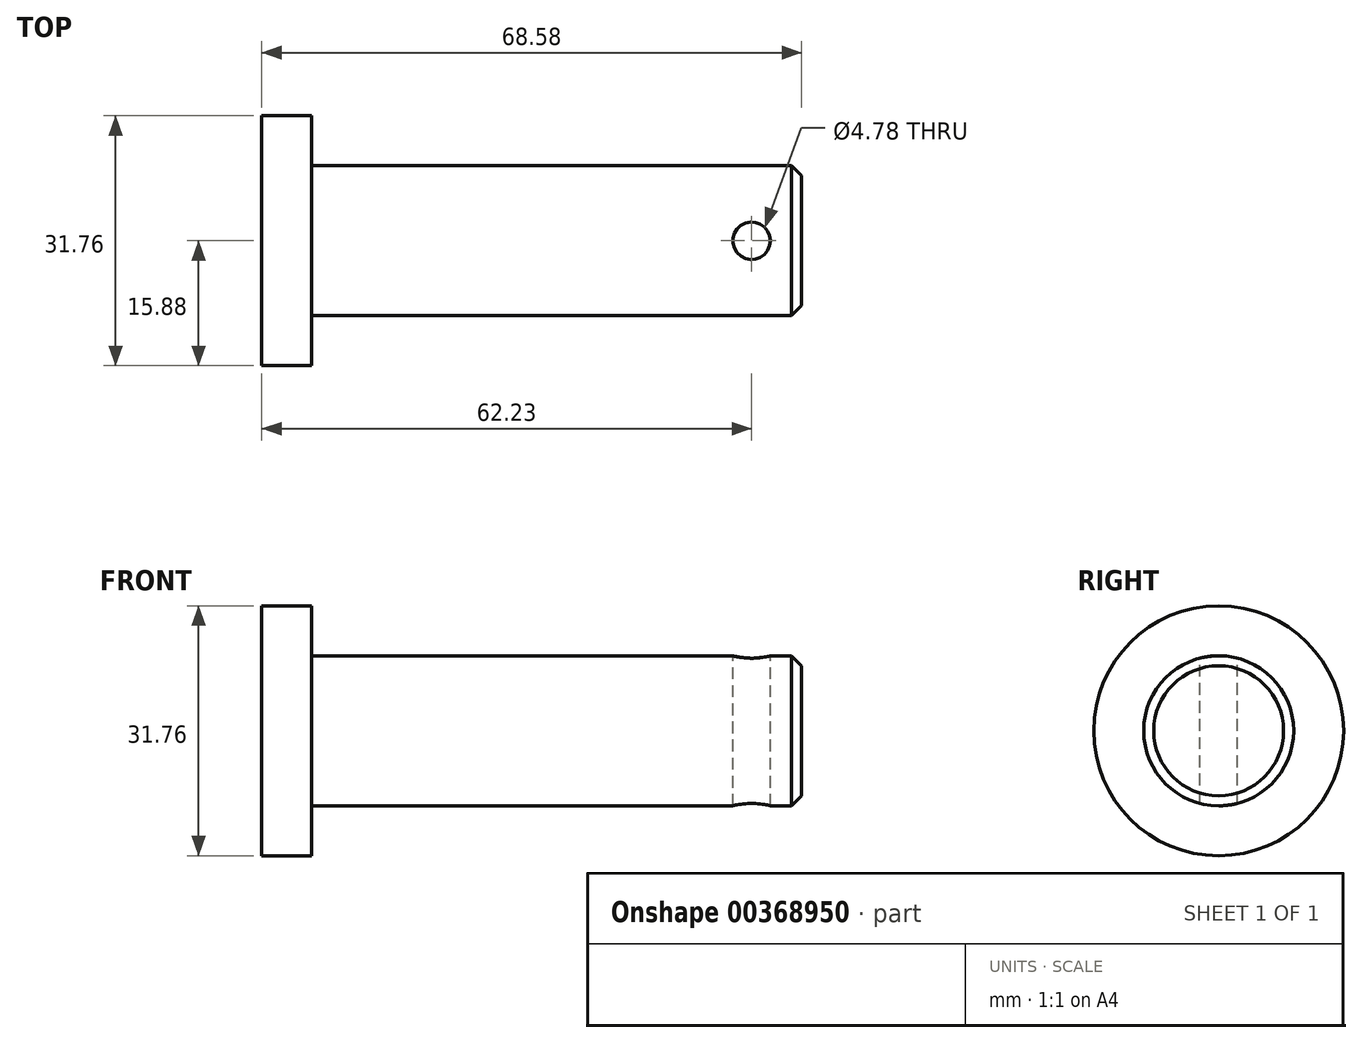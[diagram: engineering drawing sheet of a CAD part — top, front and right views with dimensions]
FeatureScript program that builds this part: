
annotation { "Feature Type Name" : "Feature", "Feature Type Description" : "" }
export const myFeature = defineFeature(function(context is Context, id is Id, definition is map)
    precondition{}
    {
        {
            var Q0;
            Q0=qCreatedBy(makeId("Right.planeOp"),FACE);
            var sketch = newSketch(context, id + "F0", { "sketchPlane" : qUnion([Q0])});
            skCircle(sketch, "E0", {"center": v(0, 0) * mm, "radius": 15.88 * mm});
            skCircle(sketch, "E1", {"center": v(0, 0) * mm, "radius": 9.53 * mm});
            skSolve(sketch);
        }
        {
            var Q0;
            Q0 = qSketchRegion(id + "F0", true);
            extrude(context, id + "F1", {"entities" : qUnion([Q0]), "depth" : 6.35 * mm});
        }
        {
            var Q0;
            Q0=makeQuery(id+"F0.imprint","IMPRINT",FACE,{"disambiguationData":[TD([[makeQuery(id+"F0.imprint","IMPRINT",EDGE,{"derivedFrom":sQuery(id+"F0.wireOp",EDGE,"E1")}),1.0]])]});
            extrude(context, id + "F2", {"entities" : qUnion([Q0]), "operationType" : NewBodyOperationType.ADD, "depth" : 68.58 * mm});
        }
        {
            var Q0;
            Q0=makeQuery(id+"F2.opExtrude","CAP_EDGE",EDGE,{"disambiguationData":[OSD([sQuery(id+"F0.wireOp",EDGE,"E1")])],"isStart":false});
            chamfer(context, id + "F3", {"entities" : qUnion([Q0]), "chamferType" : ChamferType.OFFSET_ANGLE, "width" : 1.27 * mm, "oppositeDirection" : false, "angle" : 45 * degree, "tangentPropagation" : true});
        }
        {
            var Q0;
            Q0=qCreatedBy(makeId("Top.planeOp"),FACE);
            cPlane(context, id + "F4", {"entities" : qUnion([Q0]), "cplaneType" : CPlaneType.OFFSET, "offset" : 9.52 * mm, "width" : 152.4 * mm, "height" : 152.4 * mm});
        }
        {
            var Q0;
            Q0=qCreatedBy(id+"F4.planeOp",FACE);
            var sketch = newSketch(context, id + "F5", { "sketchPlane" : qUnion([Q0])});
            skCircle(sketch, "E2", {"center": v(62.23, 0) * mm, "radius": 2.39 * mm});
            skLineSegment(sketch, "E3.0", {"start": v(68.58, 8.26) * mm, "end": v(68.58, -8.26) * mm});
            skSolve(sketch);
        }
        {
            var Q0;
            Q0 = qSketchRegion(id + "F5", true);
            extrude(context, id + "F6", {"entities" : qUnion([Q0]), "operationType" : NewBodyOperationType.REMOVE, "endBound" : BoundingType.THROUGH_ALL, "oppositeDirection" : true, "depth" : 25.4 * mm});
        }
    });
